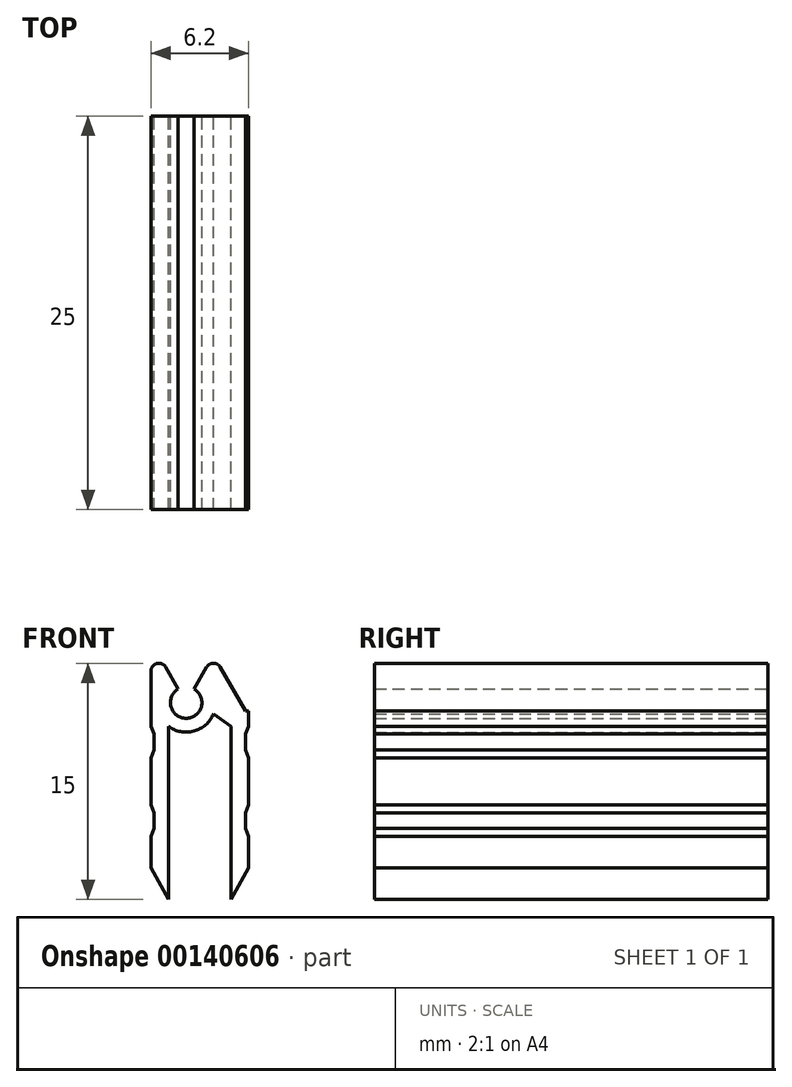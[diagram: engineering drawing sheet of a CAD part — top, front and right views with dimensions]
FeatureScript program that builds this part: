
annotation { "Feature Type Name" : "Feature", "Feature Type Description" : "" }
export const myFeature = defineFeature(function(context is Context, id is Id, definition is map)
    precondition{}
    {
        {
            var Q0;
            Q0=qCreatedBy(makeId("Front.planeOp"),FACE);
            var sketch = newSketch(context, id + "F0", { "sketchPlane" : qUnion([Q0])});
            skLineSegment(sketch, "E0.bottom", {"start": v(-3.1, -7.5) * mm, "end": v(3.1, -7.5) * mm, "construction": true});
            skLineSegment(sketch, "E0.top", {"start": v(-3.1, 7.5) * mm, "end": v(3.1, 7.5) * mm, "construction": true});
            skLineSegment(sketch, "E0.left", {"start": v(-3.1, -7.5) * mm, "end": v(-3.1, 7.5) * mm, "construction": true});
            skLineSegment(sketch, "E0.right", {"start": v(3.1, -7.5) * mm, "end": v(3.1, 7.5) * mm, "construction": true});
            skPoint(sketch, "E0.middle", {"position": v(0, 0) * mm});
            skLineSegment(sketch, "E1", {"start": v(-2, 3.5) * mm, "end": v(-2, -7.5) * mm});
            skLineSegment(sketch, "E2", {"start": v(-2, -7.5) * mm, "end": v(-3.1, -5.5) * mm});
            skLineSegment(sketch, "E3", {"start": v(-3.1, -5.5) * mm, "end": v(-3.1, -3.5) * mm});
            skLineSegment(sketch, "E4", {"start": v(-3.1, -3.5) * mm, "end": v(-2.9, -3) * mm});
            skLineSegment(sketch, "E5", {"start": v(-2.9, -3) * mm, "end": v(-2.9, -2) * mm});
            skLineSegment(sketch, "E6", {"start": v(-2.9, -2) * mm, "end": v(-3.1, -1.5) * mm});
            skLineSegment(sketch, "E7", {"start": v(-3.1, -1.5) * mm, "end": v(-3.1, 1.5) * mm});
            skLineSegment(sketch, "E8", {"start": v(-3.1, 1.5) * mm, "end": v(-2.9, 2) * mm});
            skLineSegment(sketch, "E9", {"start": v(-2.9, 2) * mm, "end": v(-2.9, 3) * mm});
            skLineSegment(sketch, "E10", {"start": v(-2.9, 3) * mm, "end": v(-3.1, 3.5) * mm});
            skLineSegment(sketch, "E11", {"start": v(-3.1, 3.5) * mm, "end": v(-3.1, 7) * mm});
            skLineSegment(sketch, "E12", {"start": v(-2.17, 7.25) * mm, "end": v(-0.87, 5) * mm});
            skPoint(sketch, "E13.visualSharp", {"position": v(-3.1, 8.87) * mm});
            skArc(sketch, "E13.filletArc", {"start": v(-2.17, 7.25) * mm, "mid": v(-2.73, 7.48) * mm, "end": v(-3.1, 7) * mm});
            skLineSegment(sketch, "E14", {"start": v(-0.87, 5) * mm, "end": v(0.43, 7.25) * mm});
            skLineSegment(sketch, "E15", {"start": v(1.3, 7.25) * mm, "end": v(2.9, 4.48) * mm});
            skLineSegment(sketch, "E16", {"start": v(2.9, 4.48) * mm, "end": v(3.1, 4.48) * mm});
            skPoint(sketch, "E17.visualSharp", {"position": v(0.87, 8) * mm});
            skArc(sketch, "E17.filletArc", {"start": v(1.3, 7.25) * mm, "mid": v(0.87, 7.5) * mm, "end": v(0.43, 7.25) * mm});
            skLineSegment(sketch, "E18", {"start": v(-0.87, 5) * mm, "end": v(-0.87, 4.27) * mm, "construction": true});
            skLineSegment(sketch, "E19", {"start": v(0.87, 7) * mm, "end": v(0.87, 4.27) * mm, "construction": true});
            skArc(sketch, "E20", {"start": v(-1.37, 5.86) * mm, "mid": v(-0.87, 4) * mm, "end": v(-0.37, 5.86) * mm});
            skLineSegment(sketch, "E21", {"start": v(0, 0) * mm, "end": v(0, -7.5) * mm, "construction": true});
            skLineSegment(sketch, "E22.MirrorCS", {"start": v(2.9, 3) * mm, "end": v(3.1, 3.5) * mm});
            skLineSegment(sketch, "E23.MirrorCS", {"start": v(2.9, 2) * mm, "end": v(2.9, 3) * mm});
            skLineSegment(sketch, "E24.MirrorCS", {"start": v(3.1, 1.5) * mm, "end": v(2.9, 2) * mm});
            skLineSegment(sketch, "E25.MirrorCS", {"start": v(3.1, -1.5) * mm, "end": v(3.1, 1.5) * mm});
            skLineSegment(sketch, "E26.MirrorCS", {"start": v(2.9, -2) * mm, "end": v(3.1, -1.5) * mm});
            skLineSegment(sketch, "E27.MirrorCS", {"start": v(2.9, -3) * mm, "end": v(2.9, -2) * mm});
            skLineSegment(sketch, "E28.MirrorCS", {"start": v(3.1, -3.5) * mm, "end": v(2.9, -3) * mm});
            skLineSegment(sketch, "E29.MirrorCS", {"start": v(3.1, -5.5) * mm, "end": v(3.1, -3.5) * mm});
            skLineSegment(sketch, "E30.MirrorCS", {"start": v(2, -7.5) * mm, "end": v(3.1, -5.5) * mm});
            skLineSegment(sketch, "E31.MirrorCS", {"start": v(2, 3.5) * mm, "end": v(2, -7.5) * mm});
            skArc(sketch, "E32", {"start": v(-2, 3.5) * mm, "mid": v(-0.38, 3.18) * mm, "end": v(0.87, 4.27) * mm});
            skLineSegment(sketch, "E33", {"start": v(0.87, 4.27) * mm, "end": v(2, 3.5) * mm});
            skLineSegment(sketch, "E34", {"start": v(3.1, 4.48) * mm, "end": v(3.1, 3.5) * mm});
            skLineSegment(sketch, "E35", {"start": v(-0.87, 5) * mm, "end": v(-3.1, 5) * mm, "construction": true});
            skLineSegment(sketch, "E36", {"start": v(0.87, 7) * mm, "end": v(3.1, 7) * mm, "construction": true});
            skSolve(sketch);
        }
        {
            var Q0;
            Q0=makeQuery(id+"F0.imprint","IMPRINT",FACE,{"disambiguationData":[TD([[makeQuery(id+"F0.imprint","IMPRINT",EDGE,{"derivedFrom":sQuery(id+"F0.wireOp",EDGE,"E1")}),-1.0]])]});
            extrude(context, id + "F1", {"entities" : qUnion([Q0]), "depth" : 25 * mm, "offsetDistance" : 25 * mm});
        }
    });
